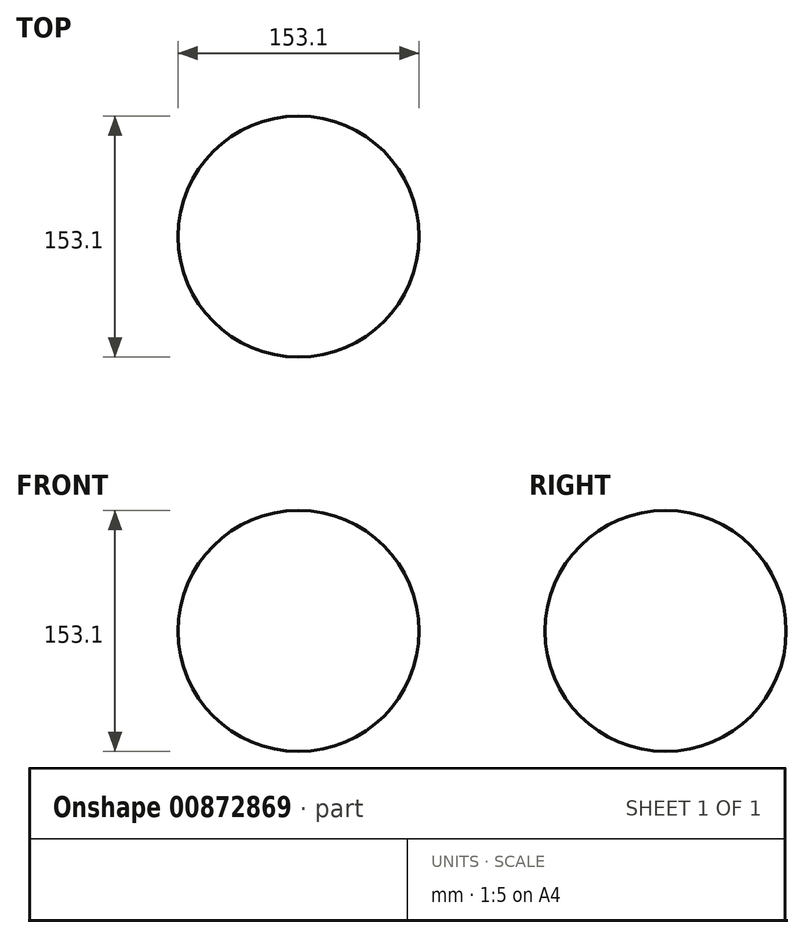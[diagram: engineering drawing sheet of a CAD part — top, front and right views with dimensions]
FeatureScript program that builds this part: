
annotation { "Feature Type Name" : "Feature", "Feature Type Description" : "" }
export const myFeature = defineFeature(function(context is Context, id is Id, definition is map)
    precondition{}
    {
        {
            var Q0;
            Q0=qCreatedBy(makeId("Front.planeOp"),FACE);
            var sketch = newSketch(context, id + "F0", { "sketchPlane" : qUnion([Q0])});
            skArc(sketch, "E0", {"start": v(0, 76.55) * mm, "mid": v(-76.55, 0) * mm, "end": v(0, -76.55) * mm});
            skSolve(sketch);
        }
        {
            var Q0;
            Q0=qCreatedBy(makeId("Front.planeOp"),FACE);
            var sketch = newSketch(context, id + "F1", { "sketchPlane" : qUnion([Q0])});
            skLineSegment(sketch, "E1", {"start": v(0, -76.1) * mm, "end": v(0, 75.9) * mm});
            skSolve(sketch);
        }
        {
            var Q0;
            Q0=sQuery(id+"F0.wireOp",EDGE,"E0");
            var Q1;
            Q1=sQuery(id+"F1.wireOp",EDGE,"E1");
            revolve(context, id + "F2", {"bodyType" : ToolBodyType.SURFACE, "surfaceOperationType" : NewSurfaceOperationType.NEW, "surfaceEntities" : qUnion([Q0]), "axis" : qUnion([Q1]), "revolveType" : RevolveType.FULL});
        }
    });
